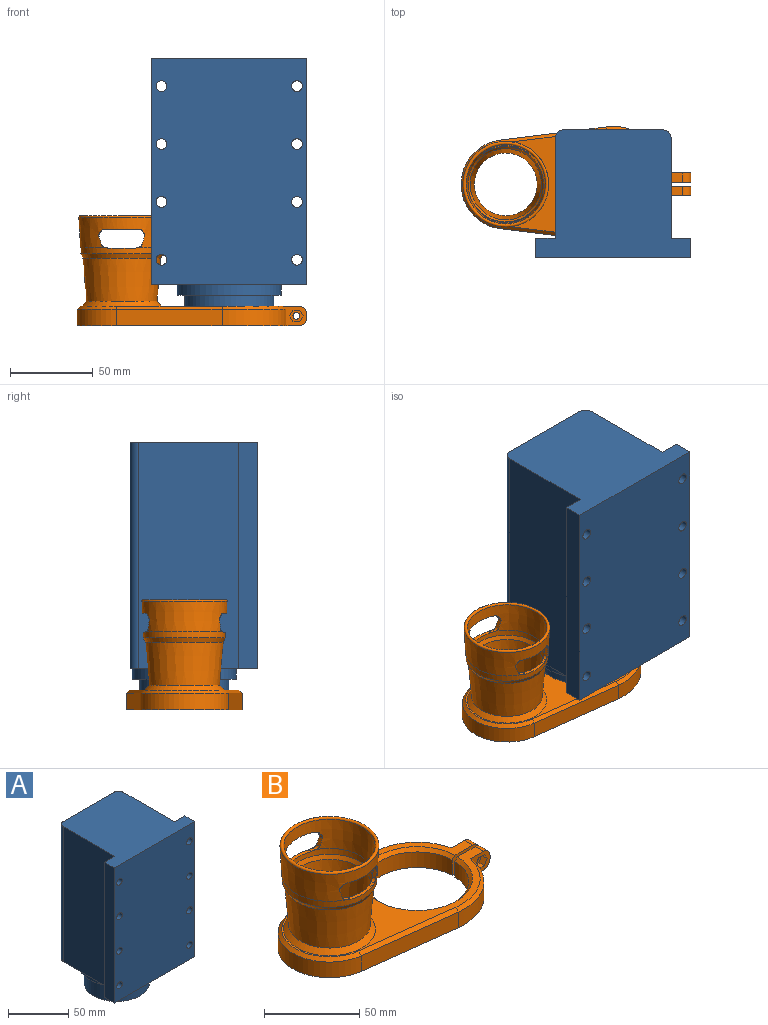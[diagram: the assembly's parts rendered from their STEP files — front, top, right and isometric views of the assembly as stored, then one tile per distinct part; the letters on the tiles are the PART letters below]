
ASSEMBLY  parts=2 mates=1
PART A: 24 faces, bbox 94x77x162 mm
  f0: plane 137x94mm, normal (0,-1,0), area 12612.5mm2, adj f2,f3,f10,f11,f12,f13,f14,f15
  f1: plane 137x12mm, normal (0,1,0), area 1511.3mm2, adj f2,f9,f10,f11,f16,f17,f18,f19
  f2: plane 137x11.5mm, normal (-1,0,0), area 1575.5mm2, adj f0,f1,f10,f11
  f3: plane 137x11.5mm, normal (1,0,0), area 1575.5mm2, adj f0,f4,f10,f11
  f4: plane 137x12mm, normal (0,1,0), area 1511.3mm2, adj f3,f5,f10,f11,f12,f13,f14,f15
  f5: plane 137x60.5mm, normal (1,0,0), area 8288.5mm2, adj f4,f6,f10,f11
  f6: cylinder r=5mm len=137mm, axis (0,0,-1), area 1076mm2, adj f5,f7,f10,f11
  f7: plane 137x60mm, normal (0,1,0), area 8220mm2, adj f6,f8,f10,f11
  f8: cylinder r=5mm len=137mm, axis (0,0,-1), area 1076mm2, adj f7,f9,f10,f11
  f9: plane 137x60.5mm, normal (-1,0,0), area 8288.5mm2, adj f1,f8,f10,f11
  f10: plane 94x77mm, normal (0,0,1), area 5655.3mm2, adj f0,f1,f2,f3,f4,f5,f6,f7
  f11: plane 94x77mm, normal (0,0,-1), area 2547.9mm2, adj f0,f1,f2,f3,f4,f5,f6,f7
  f12: cylinder r=3.25mm len=11.5mm, axis (0,1,0), area 234.8mm2, adj f0,f4
  f13: cylinder r=3.25mm len=11.5mm, axis (0,1,0), area 234.8mm2, adj f0,f4
  f14: cylinder r=3.25mm len=11.5mm, axis (0,1,0), area 234.8mm2, adj f0,f4
  f15: cylinder r=3.25mm len=11.5mm, axis (0,1,0), area 234.8mm2, adj f0,f4
  f16: cylinder r=3.25mm len=11.5mm, axis (0,1,0), area 234.8mm2, adj f0,f1
  f17: cylinder r=3.25mm len=11.5mm, axis (0,1,0), area 234.8mm2, adj f0,f1
  f18: cylinder r=3.25mm len=11.5mm, axis (0,1,0), area 234.8mm2, adj f0,f1
  f19: cylinder r=3.25mm len=11.5mm, axis (0,1,0), area 234.8mm2, adj f0,f1
  f20: cylinder r=31.45mm len=62.9mm, axis (0,0,1), area 1284.4mm2, adj f11,f21
  f21: plane 62.9x62.9mm, normal (0,0,-1), area 817.1mm2, adj f20,f22
  f22: cylinder r=27mm len=54mm, axis (0,0,1), area 3138.5mm2, adj f21,f23
  f23: plane 54x54mm, normal (0,0,-1), area 2290.2mm2, adj f22
PART B: 95 faces, bbox 140.1x70x66.6 mm
  f0: plane 133.99x70mm, normal (0,0,-1), area 3713.2mm2, adj f42,f44,f45,f46,f48,f49,f50,f52
  f1: cone r=23mm half-angle=3.6deg, axis (0,0,1), area 492.6mm2, adj f2,f8,f9,f18,f20,f21,f22,f23
  f2: cone r=23mm half-angle=3deg, axis (0,0,1), area 2064.2mm2, adj f1,f9,f10,f11,f12,f13,f14,f15
  f3: cone r=23.5mm half-angle=4.8deg, axis (0,0,1), area 3676.1mm2, adj f4,f89
  f4: cone r=24.75mm half-angle=26.6deg, axis (0,0,1), area 423.7mm2, adj f3,f5
  f5: cone r=25mm half-angle=3.6deg, axis (0,0,1), area 607.6mm2, adj f4,f6,f20,f21,f22,f23,f24,f25
  f6: cone r=25mm half-angle=3deg, axis (0,0,1), area 2292.7mm2, adj f5,f9,f10,f11,f12,f13,f14,f15
  f7: cone r=21.51mm half-angle=4.8deg, axis (0,0,1), area 3783.5mm2, adj f8,f43
  f8: cone r=22.96mm half-angle=26.6deg, axis (0,0,1), area 386.2mm2, adj f1,f7
  f9: cylinder r=2.5mm len=3.17mm, axis (0,-1,0), area 6mm2, adj f1,f2,f6,f10,f24
  f10: plane 4.73x3.02mm, normal (0.96,0,0.29), area 11.6mm2, adj f2,f6,f9,f11
  f11: cylinder r=2.5mm len=2.79mm, axis (0,-1,0), area 5.3mm2, adj f2,f6,f10,f12
  f12: plane 3.01x1.34mm, normal (0.83,0,-0.55), area 3.8mm2, adj f2,f6,f11,f13
  f13: cylinder r=2.5mm len=3.44mm, axis (0,-1,0), area 5.6mm2, adj f2,f6,f12,f19
  f14: cylinder r=2.5mm len=3.44mm, axis (0,-1,0), area 5.6mm2, adj f2,f6,f15,f19
  f15: plane 3.01x1.34mm, normal (-0.83,0,-0.55), area 3.8mm2, adj f2,f6,f14,f16
  f16: cylinder r=2.5mm len=2.79mm, axis (0,-1,0), area 5.3mm2, adj f2,f6,f15,f17
  f17: plane 4.73x3.02mm, normal (-0.96,0,0.29), area 11.6mm2, adj f2,f6,f16,f18
  f18: cylinder r=2.5mm len=3.17mm, axis (0,-1,0), area 6mm2, adj f1,f2,f6,f17,f20
  f19: plane 20.86x4.44mm, normal (0,0,-1), area 43.1mm2, adj f2,f6,f13,f14
  f20: plane 3.07x2.15mm, normal (-0.22,0,0.98), area 4.8mm2, adj f1,f5,f6,f18,f21
  f21: cylinder r=2.5mm len=2.32mm, axis (0,-1,0), area 1.2mm2, adj f1,f5,f20,f22
  f22: plane 15.55x3.36mm, normal (0,0,1), area 31.7mm2, adj f1,f5,f21,f23
  f23: cylinder r=2.5mm len=2.32mm, axis (0,-1,0), area 1.2mm2, adj f1,f5,f22,f24
  f24: plane 3.07x2.15mm, normal (0.22,0,0.98), area 4.8mm2, adj f1,f5,f6,f9,f23
  f25: plane 3.07x2.15mm, normal (0.22,0,0.98), area 4.8mm2, adj f1,f5,f6,f26,f35
  f26: cylinder r=2.5mm len=2.32mm, axis (0,-1,0), area 1.2mm2, adj f1,f5,f25,f27
  f27: plane 15.55x3.36mm, normal (0,0,1), area 31.7mm2, adj f1,f5,f26,f28
  f28: cylinder r=2.5mm len=2.32mm, axis (0,-1,0), area 1.2mm2, adj f1,f5,f27,f29
  f29: plane 3.07x2.15mm, normal (-0.22,0,0.98), area 4.8mm2, adj f1,f5,f6,f28,f36
  f30: plane 20.86x4.44mm, normal (0,0,-1), area 43.1mm2, adj f2,f6,f31,f40
  f31: cylinder r=2.5mm len=3.44mm, axis (0,-1,0), area 5.6mm2, adj f2,f6,f30,f32
  f32: plane 3.01x1.34mm, normal (0.83,0,-0.55), area 3.8mm2, adj f2,f6,f31,f33
  f33: cylinder r=2.5mm len=2.79mm, axis (0,-1,0), area 5.3mm2, adj f2,f6,f32,f34
  f34: plane 4.73x3.02mm, normal (0.96,0,0.29), area 11.6mm2, adj f2,f6,f33,f35
  f35: cylinder r=2.5mm len=3.17mm, axis (0,-1,0), area 6mm2, adj f1,f2,f6,f25,f34
  f36: cylinder r=2.5mm len=3.17mm, axis (0,-1,0), area 6mm2, adj f1,f2,f6,f29,f37
  f37: plane 4.73x3.02mm, normal (-0.96,0,0.29), area 11.6mm2, adj f2,f6,f36,f38
  f38: cylinder r=2.5mm len=2.79mm, axis (0,-1,0), area 5.3mm2, adj f2,f6,f37,f39
  f39: plane 3.01x1.34mm, normal (-0.83,0,-0.55), area 3.8mm2, adj f2,f6,f38,f40
  f40: cylinder r=2.5mm len=3.44mm, axis (0,-1,0), area 5.6mm2, adj f2,f6,f30,f39
  f41: torus R=24.95mm, axis (0,0,-1), area 493.1mm2, adj f2,f6
  f42: cylinder r=19.01mm len=38.01mm, axis (0,0,1), area 1433.1mm2, adj f0,f43
  f43: plane 38.15x38.15mm, normal (0,0,1), area 8.3mm2, adj f7,f42
  f44: plane 64.02x10mm, normal (-0.12,-0.99,0), area 645.1mm2, adj f0,f45,f55,f91
  f45: cylinder r=35mm len=38.6mm, axis (0,0,1), area 522.5mm2, adj f0,f44,f46,f90
  f46: plane 14.75x12.01mm, normal (0,-1,0), area 98.7mm2, adj f0,f45,f47,f56,f57,f58,f59,f60
  f47: plane 6x2mm, normal (1,0,0), area 12mm2, adj f46,f48,f85,f87
  f48: plane 20x12mm, normal (0,1,0), area 214.1mm2, adj f0,f47,f49,f56,f64,f85,f87,f88
  f49: cylinder r=27mm len=54mm, axis (0,0,1), area 1676.5mm2, adj f0,f48,f50,f88
  f50: plane 20x12mm, normal (0,-1,0), area 214.1mm2, adj f0,f49,f51,f56,f65,f84,f86,f88
  f51: plane 6x2mm, normal (1,0,0), area 12mm2, adj f50,f52,f84,f86
  f52: plane 14.75x12.01mm, normal (0,1,0), area 130.4mm2, adj f0,f51,f53,f56,f65,f84,f86,f94
  f53: cylinder r=35mm len=38.6mm, axis (0,0,1), area 522.5mm2, adj f0,f52,f54,f94
  f54: plane 64.02x10mm, normal (-0.12,0.99,0), area 645.1mm2, adj f0,f53,f55,f93
  f55: cylinder r=27.01mm len=53.6mm, axis (0,0,1), area 781.9mm2, adj f0,f44,f54,f92
  f56: plane 131.99x66mm, normal (0,0,1), area 2130.9mm2, adj f46,f48,f50,f52,f84,f85,f88,f89
  f57: plane 4x3.6mm, normal (-0.87,0,0.5), area 16.6mm2, adj f46,f58,f62,f63
  f58: plane 4x3.6mm, normal (-0.87,0,-0.5), area 16.6mm2, adj f46,f57,f59,f63
  f59: plane 4.16x4mm, normal (0,0,-1), area 16.6mm2, adj f46,f58,f60,f63
  f60: plane 4x3.6mm, normal (0.87,0,-0.5), area 16.6mm2, adj f46,f59,f61,f63
  f61: plane 4x3.6mm, normal (0.87,0,0.5), area 16.6mm2, adj f46,f60,f62,f63
  f62: plane 4.16x4mm, normal (0,0,1), area 16.6mm2, adj f46,f57,f61,f63
  f63: plane 8.31x7.2mm, normal (0,-1,0), area 31.7mm2, adj f57,f58,f59,f60,f61,f62,f64
  f64: cylinder r=2.05mm len=4.1mm, axis (0,-1,0), area 25.8mm2, adj f48,f63
  f65: cylinder r=2.05mm len=6mm, axis (0,-1,0), area 77.3mm2, adj f50,f52
  f66: cylinder r=1.5mm len=3mm, axis (0,0,-1), area 14.1mm2, adj f0,f67
  f67: plane 3x3mm, normal (0,0,-1), area 7.1mm2, adj f66
  f68: cylinder r=1.5mm len=3mm, axis (0,0,-1), area 14.1mm2, adj f0,f69
  f69: plane 3x3mm, normal (0,0,-1), area 7.1mm2, adj f68
  f70: cylinder r=1.5mm len=3mm, axis (0,0,-1), area 14.1mm2, adj f0,f71
  f71: plane 3x3mm, normal (0,0,-1), area 7.1mm2, adj f70
  f72: cylinder r=1.5mm len=3mm, axis (0,0,-1), area 14.1mm2, adj f0,f73
  f73: plane 3x3mm, normal (0,0,-1), area 7.1mm2, adj f72
  f74: cylinder r=1.5mm len=3mm, axis (0,0,-1), area 14.1mm2, adj f0,f75
  f75: plane 3x3mm, normal (0,0,-1), area 7.1mm2, adj f74
  f76: cylinder r=1.5mm len=3mm, axis (0,0,-1), area 14.1mm2, adj f0,f77
  f77: plane 3x3mm, normal (0,0,-1), area 7.1mm2, adj f76
  f78: cylinder r=1.5mm len=3mm, axis (0,0,-1), area 14.1mm2, adj f0,f79
  f79: plane 3x3mm, normal (0,0,-1), area 7.1mm2, adj f78
  f80: cylinder r=1.5mm len=3mm, axis (0,0,-1), area 14.1mm2, adj f0,f81
  f81: plane 3x3mm, normal (0,0,-1), area 7.1mm2, adj f80
  f82: cylinder r=1.5mm len=3mm, axis (0,0,-1), area 14.1mm2, adj f0,f83
  f83: plane 3x3mm, normal (0,0,-1), area 7.1mm2, adj f82
  f84: cylinder r=5mm len=6mm, axis (0,1,0), area 47.1mm2, adj f50,f51,f52,f56
  f85: cylinder r=5mm len=6mm, axis (0,1,0), area 47.1mm2, adj f46,f47,f48,f56
  f86: cylinder r=5mm len=6mm, axis (0,-1,0), area 47.1mm2, adj f0,f50,f51,f52
  f87: cylinder r=5mm len=6mm, axis (0,-1,0), area 47.1mm2, adj f0,f46,f47,f48
  f88: cone r=27mm half-angle=45deg, axis (0,0,1), area 491.9mm2, adj f48,f49,f50,f56
  f89: cone r=24.08mm half-angle=42.6deg, axis (0,0,-1), area 579.7mm2, adj f3,f56
  f90: cone r=33mm half-angle=45deg, axis (0,0,-1), area 143mm2, adj f45,f46,f56,f91
  f91: plane 64.26x9.92mm, normal (-0.09,-0.7,0.71), area 182.5mm2, adj f44,f56,f90,f92
  f92: cone r=25.01mm half-angle=45deg, axis (0,0,-1), area 213mm2, adj f55,f56,f91,f93
  f93: plane 64.26x9.92mm, normal (-0.09,0.7,0.71), area 182.5mm2, adj f54,f56,f92,f94
  f94: cone r=33mm half-angle=45deg, axis (0,0,-1), area 143mm2, adj f52,f53,f56,f93
PLACE A t=(-54.25,25.36,0.07)mm
PLACE B t=(-119.25,25.36,22.57)mm
MATE revolute B.f49 <-> A.f22  axis (0,0,1) through (-54.25,25.36,-24.93)mm
